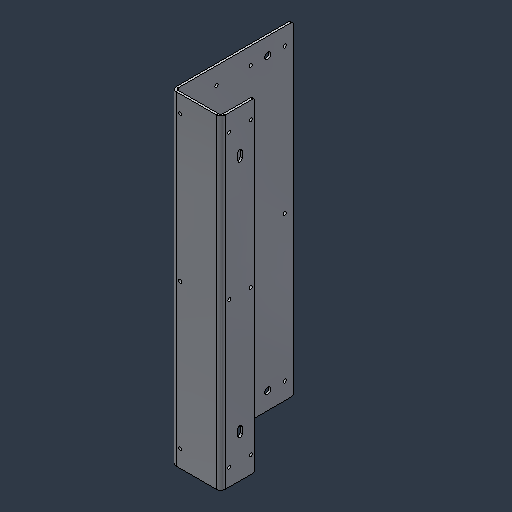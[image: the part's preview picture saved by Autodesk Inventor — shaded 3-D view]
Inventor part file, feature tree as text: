
AUTODESK INVENTOR PART (.ipt)
format: ipt  version: 2024.3 (Build 283343000, 343)  size: 120,320 bytes
history: native  units: mm (DEFAULTED — no unit token found)
features: fillet x1
ambient origin geometry x8: Origin, YZ Plane, XZ Plane, XY Plane, X Axis, Y Axis, Z Axis, Center Point
bodies: Solid1 (feature_tree)
feature tree (1):
  fillet  "Fillet1"  [1 undecoded]
note: 1 required parameter value undecoded (feature->parameter linkage not recoverable at this tier; creation-order binding heuristic only, values carry confidence <= 0.55)
